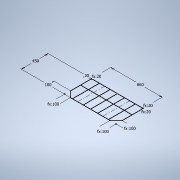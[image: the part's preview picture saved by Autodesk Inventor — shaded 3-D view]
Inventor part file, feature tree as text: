
AUTODESK INVENTOR PART (.ipt)
format: ipt  version: 2022.1 (Build 261234000, 234)  size: 103,424 bytes
history: native  units: mm
features: sketch x2
ambient origin geometry x8: Origin, YZ Plane, XZ Plane, XY Plane, X Axis, Y Axis, Z Axis, Center Point
feature tree (2):
  sketch  "Sketch1"  dims[d23=100.0mm]
  sketch  "Sketch2"  dims[d24=100.0mm d25=100.0mm d26=100.0mm d27=20.0mm d28=20.0mm d29=20.0mm d30=20.0mm d31=450.0mm]
